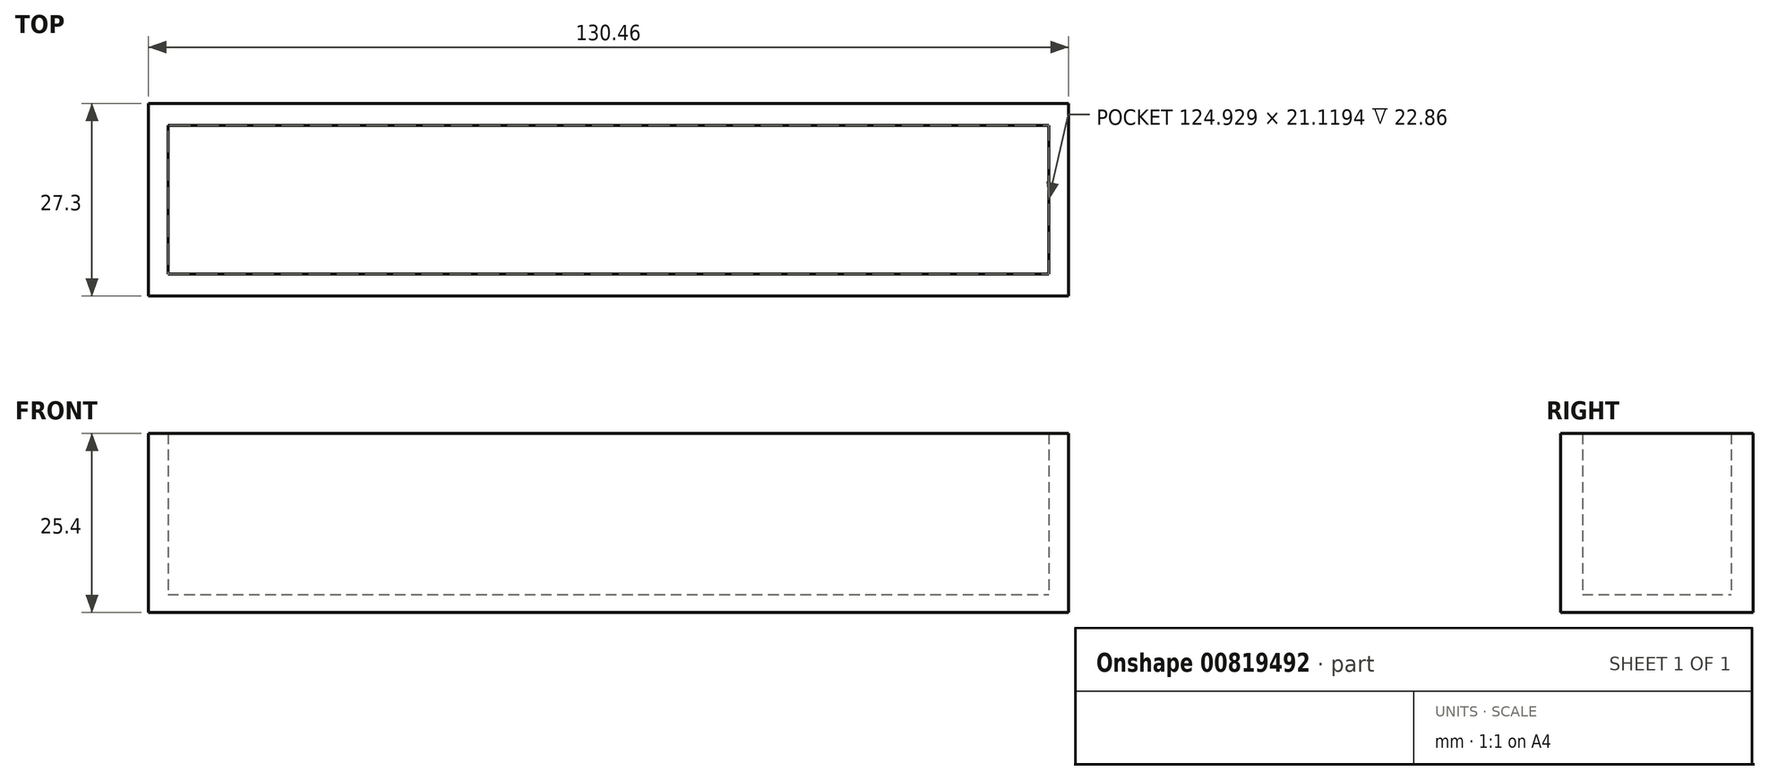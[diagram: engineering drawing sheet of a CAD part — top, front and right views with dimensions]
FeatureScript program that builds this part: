
annotation { "Feature Type Name" : "Feature", "Feature Type Description" : "" }
export const myFeature = defineFeature(function(context is Context, id is Id, definition is map)
    precondition{}
    {
        {
            var Q0;
            Q0=qCreatedBy(makeId("Top.planeOp"),FACE);
            var sketch = newSketch(context, id + "F0", { "sketchPlane" : qUnion([Q0])});
            skLineSegment(sketch, "E0.bottom", {"start": v(-65.23, -13.65) * mm, "end": v(65.23, -13.65) * mm});
            skLineSegment(sketch, "E0.top", {"start": v(-65.23, 13.65) * mm, "end": v(65.23, 13.65) * mm});
            skLineSegment(sketch, "E0.left", {"start": v(-65.23, -13.65) * mm, "end": v(-65.23, 13.65) * mm});
            skLineSegment(sketch, "E0.right", {"start": v(65.23, -13.65) * mm, "end": v(65.23, 13.65) * mm});
            skPoint(sketch, "E0.middle", {"position": v(0, 0) * mm});
            skLineSegment(sketch, "E1.bottom", {"start": v(-62.46, -10.56) * mm, "end": v(62.46, -10.56) * mm});
            skLineSegment(sketch, "E1.top", {"start": v(-62.46, 10.56) * mm, "end": v(62.46, 10.56) * mm});
            skLineSegment(sketch, "E1.left", {"start": v(-62.46, -10.56) * mm, "end": v(-62.46, 10.56) * mm});
            skLineSegment(sketch, "E1.right", {"start": v(62.46, -10.56) * mm, "end": v(62.46, 10.56) * mm});
            skLineSegment(sketch, "E2", {"start": v(-62.46, 10.56) * mm, "end": v(-65.23, 13.65) * mm});
            skLineSegment(sketch, "E3", {"start": v(-65.23, -13.65) * mm, "end": v(-62.46, -10.56) * mm});
            skLineSegment(sketch, "E4", {"start": v(62.46, -10.56) * mm, "end": v(65.23, -13.65) * mm});
            skLineSegment(sketch, "E5", {"start": v(62.46, 10.56) * mm, "end": v(65.23, 13.65) * mm});
            skSolve(sketch);
        }
        {
            var Q0;
            Q0=makeQuery(id+"F0.imprint","IMPRINT",FACE,{"disambiguationData":[TD([[makeQuery(id+"F0.imprint","IMPRINT",EDGE,{"derivedFrom":sQuery(id+"F0.wireOp",EDGE,"E0.left")}),-1.0]])]});
            var Q1;
            Q1=makeQuery(id+"F0.imprint","IMPRINT",FACE,{"disambiguationData":[TD([[makeQuery(id+"F0.imprint","IMPRINT",EDGE,{"derivedFrom":sQuery(id+"F0.wireOp",EDGE,"E0.bottom")}),1.0]])]});
            var Q2;
            Q2=makeQuery(id+"F0.imprint","IMPRINT",FACE,{"disambiguationData":[TD([[makeQuery(id+"F0.imprint","IMPRINT",EDGE,{"derivedFrom":sQuery(id+"F0.wireOp",EDGE,"E0.top")}),-1.0]])]});
            var Q3;
            Q3=makeQuery(id+"F0.imprint","IMPRINT",FACE,{"disambiguationData":[TD([[makeQuery(id+"F0.imprint","IMPRINT",EDGE,{"derivedFrom":sQuery(id+"F0.wireOp",EDGE,"E0.right")}),1.0]])]});
            extrude(context, id + "F1", {"entities" : qUnion([Q0, Q1, Q2, Q3]), "depth" : 25.4 * mm, "offsetDistance" : 25.4 * mm});
        }
        {
            var Q0;
            Q0=qCreatedBy(makeId("Top.planeOp"),FACE);
            var sketch = newSketch(context, id + "F2", { "sketchPlane" : qUnion([Q0])});
            skLineSegment(sketch, "E6.bottom", {"start": v(-65.23, 13.48) * mm, "end": v(65.23, 13.48) * mm});
            skLineSegment(sketch, "E6.top", {"start": v(-65.23, -13.48) * mm, "end": v(65.23, -13.48) * mm});
            skLineSegment(sketch, "E6.left", {"start": v(-65.23, 13.48) * mm, "end": v(-65.23, -13.48) * mm});
            skLineSegment(sketch, "E6.right", {"start": v(65.23, 13.48) * mm, "end": v(65.23, -13.48) * mm});
            skPoint(sketch, "E6.middle", {"position": v(0, 0) * mm});
            skSolve(sketch);
        }
        {
            var Q0;
            Q0=makeQuery(id+"F2.imprint","IMPRINT",FACE,{"disambiguationData":[TD([[makeQuery(id+"F2.imprint","IMPRINT",EDGE,{"derivedFrom":sQuery(id+"F2.wireOp",EDGE,"E6.bottom")}),-1.0]])]});
            extrude(context, id + "F3", {"entities" : qUnion([Q0]), "operationType" : NewBodyOperationType.ADD, "depth" : 2.54 * mm, "offsetDistance" : 25.4 * mm});
        }
    });
